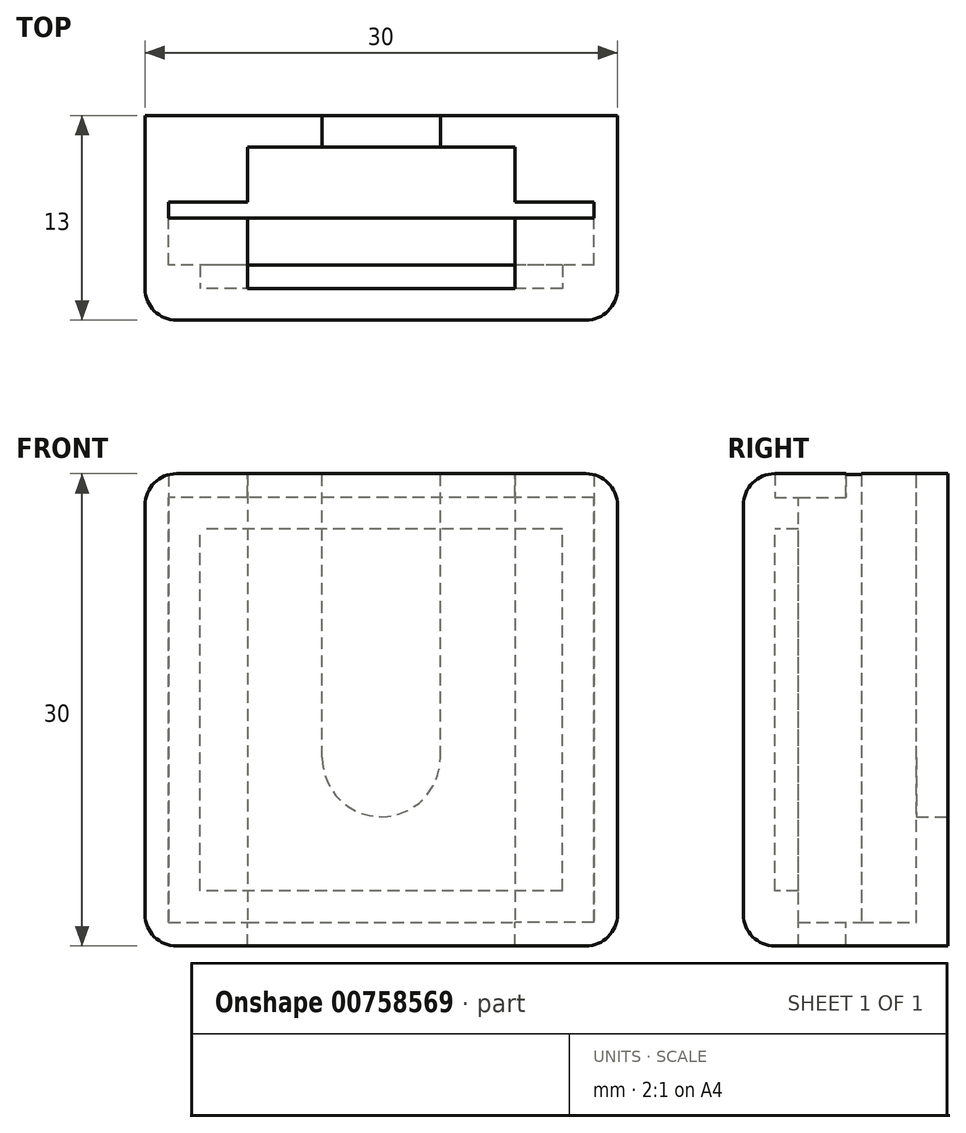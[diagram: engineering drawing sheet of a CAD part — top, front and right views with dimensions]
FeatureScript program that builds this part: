
annotation { "Feature Type Name" : "Feature", "Feature Type Description" : "" }
export const myFeature = defineFeature(function(context is Context, id is Id, definition is map)
    precondition{}
    {
        {
            var Q0;
            Q0=qCreatedBy(makeId("Front.planeOp"),FACE);
            var sketch = newSketch(context, id + "F0", { "sketchPlane" : qUnion([Q0])});
            skLineSegment(sketch, "E0.bottom", {"start": v(13.5, -13.5) * mm, "end": v(-13.5, -13.5) * mm});
            skLineSegment(sketch, "E0.top", {"start": v(13.5, 13.5) * mm, "end": v(-13.5, 13.5) * mm});
            skLineSegment(sketch, "E0.left", {"start": v(13.5, -13.5) * mm, "end": v(13.5, 13.5) * mm});
            skLineSegment(sketch, "E0.right", {"start": v(-13.5, -13.5) * mm, "end": v(-13.5, 13.5) * mm});
            skPoint(sketch, "E0.middle", {"position": v(0, 0) * mm});
            skLineSegment(sketch, "E1.0", {"start": v(15, 15) * mm, "end": v(-15, 15) * mm});
            skLineSegment(sketch, "E1.1", {"start": v(15, -15) * mm, "end": v(15, 15) * mm});
            skLineSegment(sketch, "E1.2", {"start": v(15, -15) * mm, "end": v(-15, -15) * mm});
            skLineSegment(sketch, "E1.3", {"start": v(-15, -15) * mm, "end": v(-15, 15) * mm});
            skCircle(sketch, "E2", {"center": v(0, -3.04) * mm, "radius": 3.75 * mm});
            skLineSegment(sketch, "E3", {"start": v(0, -3.04) * mm, "end": v(-3.75, -3.04) * mm, "construction": true});
            skLineSegment(sketch, "E4", {"start": v(0, -3.04) * mm, "end": v(3.75, -3.04) * mm, "construction": true});
            skLineSegment(sketch, "E5", {"start": v(3.75, -3.04) * mm, "end": v(3.75, 15) * mm});
            skLineSegment(sketch, "E6", {"start": v(-3.75, -3.04) * mm, "end": v(-3.75, 15) * mm});
            skLineSegment(sketch, "E7", {"start": v(-8.5, 15) * mm, "end": v(-8.5, -13.5) * mm});
            skLineSegment(sketch, "E8", {"start": v(8.5, 15) * mm, "end": v(8.5, -13.5) * mm});
            skSolve(sketch);
        }
        {
            var Q0;
            Q0=makeQuery(id+"F0.imprint","IMPRINT",FACE,{"disambiguationData":[TD([[makeQuery(id+"F0.imprint","IMPRINT",EDGE,{"derivedFrom":sQuery(id+"F0.wireOp",EDGE,"E0.bottom")}),-1.0]])]});
            var Q1;
            Q1=makeQuery(id+"F0.imprint","IMPRINT",FACE,{"disambiguationData":[TD([[makeQuery(id+"F0.imprint","IMPRINT",EDGE,{"derivedFrom":sQuery(id+"F0.wireOp",EDGE,"E0.bottom")}),1.0]])]});
            var Q2;
            {var subQ5=sQuery(id+"F0.wireOp",EDGE,"E7");Q2=makeQuery(id+"F0.imprint","IMPRINT",FACE,{"disambiguationData":[TD([[makeQuery(id+"F0.imprint","IMPRINT",EDGE,{"derivedFrom":subQ5}),1.0]])]});}
            var Q3;
            {var subQ0=sQuery(id+"F0.wireOp",EDGE,"E8");var subQ1=sQuery(id+"F0.wireOp",EDGE,"E0.top");var subQ2=makeQuery(id+"F0.imprint","INTERSECT",VERTEX,{"derivedFrom":[subQ1,subQ0]});Q3=makeQuery(id+"F0.imprint","IMPRINT",FACE,{"disambiguationData":[TD([[makeQuery(id+"F0.imprint","IMPRINT",EDGE,{"disambiguationData":[TD([[subQ2,-1.0]])],"derivedFrom":subQ1}),-1.0]])]});}
            var Q4;
            {var subQ10=sQuery(id+"F0.wireOp",EDGE,"E7");var subQ12=sQuery(id+"F0.wireOp",EDGE,"E0.bottom");var subQ13=makeQuery(id+"F0.imprint","INTERSECT",VERTEX,{"derivedFrom":[subQ12,subQ10]});Q4=makeQuery(id+"F0.imprint","IMPRINT",FACE,{"disambiguationData":[TD([[makeQuery(id+"F0.imprint","IMPRINT",EDGE,{"disambiguationData":[TD([[subQ13,1.0]])],"derivedFrom":subQ12}),-1.0]])]});}
            extrude(context, id + "F1", {"entities" : qUnion([Q0, Q1, Q2, Q3, Q4]), "depth" : 2 * mm, "offsetDistance" : 25 * mm});
        }
        {
            var Q0;
            {var subQ0=sQuery(id+"F0.wireOp",EDGE,"E0.right");Q0=makeQuery(id+"F0.imprint","IMPRINT",FACE,{"disambiguationData":[TD([[makeQuery(id+"F0.imprint","IMPRINT",EDGE,{"derivedFrom":subQ0}),-1.0]])]});}
            var Q1;
            {var subQ0=sQuery(id+"F0.wireOp",EDGE,"E0.left");Q1=makeQuery(id+"F0.imprint","IMPRINT",FACE,{"disambiguationData":[TD([[makeQuery(id+"F0.imprint","IMPRINT",EDGE,{"derivedFrom":subQ0}),1.0]])]});}
            var Q2;
            {var subQ5=sQuery(id+"F0.wireOp",EDGE,"E0.left");Q2=makeQuery(id+"F0.imprint","IMPRINT",FACE,{"disambiguationData":[TD([[makeQuery(id+"F0.imprint","IMPRINT",EDGE,{"derivedFrom":subQ5}),-1.0]])]});}
            extrude(context, id + "F2", {"entities" : qUnion([Q0, Q1, Q2]), "operationType" : NewBodyOperationType.ADD, "depth" : 5.5 * mm, "offsetDistance" : 25 * mm});
        }
        {
            var Q0;
            {var subQ5=sQuery(id+"F0.wireOp",EDGE,"E0.left");Q0=makeQuery(id+"F0.imprint","IMPRINT",FACE,{"disambiguationData":[TD([[makeQuery(id+"F0.imprint","IMPRINT",EDGE,{"derivedFrom":subQ5}),-1.0]])]});}
            extrude(context, id + "F3", {"entities" : qUnion([Q0]), "operationType" : NewBodyOperationType.ADD, "depth" : 11 * mm, "offsetDistance" : 25 * mm});
        }
        {
            var Q0;
            {var subQ0=sQuery(id+"F0.wireOp",EDGE,"E0.bottom");Q0=makeQuery(id+"F3.boolean.opBoolean","MERGE",FACE,{"derivedFrom":[makeQuery(id+"F2.boolean.opBoolean","MERGE",FACE,{"derivedFrom":[makeQuery(id+"F1.opExtrude","SWEPT_FACE",FACE,{"disambiguationData":[OSD([subQ0])]}),makeQuery(id+"F2.opExtrude","SWEPT_FACE",FACE,{"disambiguationData":[OSD([subQ0])]})]}),makeQuery(id+"F3.opExtrude","SWEPT_FACE",FACE,{"disambiguationData":[OSD([subQ0])]})]});}
            var sketch = newSketch(context, id + "F4", { "sketchPlane" : qUnion([Q0])});
            skLineSegment(sketch, "E9", {"start": v(-13.5, -6.5) * mm, "end": v(13.5, -6.5) * mm});
            skLineSegment(sketch, "E10", {"start": v(-8.5, -5.5) * mm, "end": v(8.5, -5.5) * mm});
            skLineSegment(sketch, "E11", {"start": v(0, -6.5) * mm, "end": v(0, -11) * mm, "construction": true});
            skLineSegment(sketch, "E12.bottom", {"start": v(8.5, -9.5) * mm, "end": v(-8.5, -9.5) * mm});
            skLineSegment(sketch, "E12.top", {"start": v(8.5, -6.5) * mm, "end": v(-8.5, -6.5) * mm});
            skLineSegment(sketch, "E12.left", {"start": v(8.5, -9.5) * mm, "end": v(8.5, -6.5) * mm});
            skLineSegment(sketch, "E12.right", {"start": v(-8.5, -9.5) * mm, "end": v(-8.5, -6.5) * mm});
            skPoint(sketch, "E12.middle", {"position": v(0, -8) * mm});
            skSolve(sketch);
        }
        {
            var Q0;
            Q0=makeQuery(id+"F4.imprint","IMPRINT",FACE,{"disambiguationData":[TD([[makeQuery(id+"F4.imprint","IMPRINT",EDGE,{"derivedFrom":sQuery(id+"F4.wireOp",EDGE,"E10")}),-1.0]])]});
            var Q1;
            {var subQ0=sQuery(id+"F0.wireOp",EDGE,"E1.0");var subQ2=makeQuery(id+"F0.imprint","IMPRINT",EDGE,{"disambiguationData":[TD([[makeQuery(id+"F0.imprint","INTERSECT",VERTEX,{"derivedFrom":[subQ0,sQuery(id+"F0.wireOp",EDGE,"E1.3")]}),1.0]])],"derivedFrom":subQ0});Q1=makeQuery(id+"F3.boolean.opBoolean","MERGE",FACE,{"derivedFrom":[makeQuery(id+"F2.boolean.opBoolean","MERGE",FACE,{"derivedFrom":[makeQuery(id+"F1.opExtrude","SWEPT_FACE",FACE,{"disambiguationData":[OSD([subQ0]),TDD([makeQuery(id+"F0.imprint","IMPRINT",EDGE,{"disambiguationData":[TD([[makeQuery(id+"F0.imprint","INTERSECT",VERTEX,{"derivedFrom":[subQ0,sQuery(id+"F0.wireOp",EDGE,"E6")]}),-1.0]])],"derivedFrom":subQ0}),subQ2])]}),makeQuery(id+"F2.opExtrude","SWEPT_FACE",FACE,{"disambiguationData":[OSD([subQ0]),TDD([subQ2])]})]}),makeQuery(id+"F3.opExtrude","SWEPT_FACE",FACE,{"disambiguationData":[OSD([subQ0]),TDD([subQ2])]})]});}
            extrude(context, id + "F5", {"entities" : qUnion([Q0]), "operationType" : NewBodyOperationType.REMOVE, "endBound" : BoundingType.UP_TO_SURFACE, "depth" : 25 * mm, "endBoundEntityFace" : qUnion([Q1]), "offsetDistance" : 25 * mm});
        }
        {
            var Q0;
            Q0=makeQuery(id+"F4.imprint","IMPRINT",FACE,{"disambiguationData":[TD([[makeQuery(id+"F4.imprint","IMPRINT",EDGE,{"derivedFrom":sQuery(id+"F4.wireOp",EDGE,"E12.bottom")}),-1.0]])]});
            var Q1;
            {var subQ0=sQuery(id+"F0.wireOp",EDGE,"E1.2");Q1=makeQuery(id+"F3.boolean.opBoolean","MERGE",FACE,{"derivedFrom":[makeQuery(id+"F2.boolean.opBoolean","MERGE",FACE,{"derivedFrom":[makeQuery(id+"F1.opExtrude","SWEPT_FACE",FACE,{"disambiguationData":[OSD([subQ0])]}),makeQuery(id+"F2.opExtrude","SWEPT_FACE",FACE,{"disambiguationData":[OSD([subQ0])]})]}),makeQuery(id+"F3.opExtrude","SWEPT_FACE",FACE,{"disambiguationData":[OSD([subQ0])]})]});}
            extrude(context, id + "F6", {"entities" : qUnion([Q0]), "operationType" : NewBodyOperationType.REMOVE, "endBound" : BoundingType.UP_TO_SURFACE, "oppositeDirection" : true, "depth" : 25 * mm, "endBoundEntityFace" : qUnion([Q1]), "offsetDistance" : 25 * mm});
        }
        {
            var Q0;
            Q0=makeQuery(id+"F3.opExtrude","CAP_FACE",FACE,{"disambiguationData":[OSD([sQuery(id+"F0.wireOp",EDGE,"E0.bottom"),sQuery(id+"F0.wireOp",EDGE,"E0.top"),sQuery(id+"F0.wireOp",EDGE,"E0.left"),sQuery(id+"F0.wireOp",EDGE,"E0.right"),sQuery(id+"F0.wireOp",EDGE,"E1.0"),sQuery(id+"F0.wireOp",EDGE,"E1.1"),sQuery(id+"F0.wireOp",EDGE,"E1.2"),sQuery(id+"F0.wireOp",EDGE,"E1.3"),sQuery(id+"F0.wireOp",EDGE,"E7"),sQuery(id+"F0.wireOp",EDGE,"E8")])],"isStart":false});
            var sketch = newSketch(context, id + "F7", { "sketchPlane" : qUnion([Q0])});
            skLineSegment(sketch, "E13.bottom", {"start": v(15, -15) * mm, "end": v(-15, -15) * mm});
            skLineSegment(sketch, "E13.top", {"start": v(15, 15) * mm, "end": v(-15, 15) * mm});
            skLineSegment(sketch, "E13.left", {"start": v(15, -15) * mm, "end": v(15, 15) * mm});
            skLineSegment(sketch, "E13.right", {"start": v(-15, -15) * mm, "end": v(-15, 15) * mm});
            skPoint(sketch, "E13.middle", {"position": v(0, 0) * mm});
            skLineSegment(sketch, "E14.bottom", {"start": v(13.5, -13.5) * mm, "end": v(-13.5, -13.5) * mm});
            skLineSegment(sketch, "E14.top", {"start": v(13.5, 13.5) * mm, "end": v(-13.5, 13.5) * mm});
            skLineSegment(sketch, "E14.left", {"start": v(13.5, -13.5) * mm, "end": v(13.5, 13.5) * mm});
            skLineSegment(sketch, "E14.right", {"start": v(-13.5, -13.5) * mm, "end": v(-13.5, 13.5) * mm});
            skLineSegment(sketch, "E15.0", {"start": v(-11.5, -11.5) * mm, "end": v(-11.5, 11.5) * mm});
            skLineSegment(sketch, "E15.1", {"start": v(11.5, -11.5) * mm, "end": v(-11.5, -11.5) * mm});
            skLineSegment(sketch, "E15.2", {"start": v(11.5, -11.5) * mm, "end": v(11.5, 11.5) * mm});
            skLineSegment(sketch, "E15.3", {"start": v(11.5, 11.5) * mm, "end": v(-11.5, 11.5) * mm});
            skSolve(sketch);
        }
        {
            var Q0;
            Q0 = qSketchRegion(id + "F7", true);
            var Q1;
            Q1=makeQuery(id+"F7.imprint","IMPRINT",FACE,{"disambiguationData":[TD([[makeQuery(id+"F7.imprint","IMPRINT",EDGE,{"derivedFrom":sQuery(id+"F7.wireOp",EDGE,"E14.bottom")}),-1.0]])]});
            var Q2;
            Q2=makeQuery(id+"F7.imprint","IMPRINT",FACE,{"disambiguationData":[TD([[makeQuery(id+"F7.imprint","IMPRINT",EDGE,{"derivedFrom":sQuery(id+"F7.wireOp",EDGE,"E15.0")}),-1.0]])]});
            extrude(context, id + "F8", {"entities" : qUnion([Q0, Q1, Q2]), "depth" : 2 * mm, "offsetDistance" : 25 * mm});
        }
        {
            var Q0;
            Q0=makeQuery(id+"F7.imprint","IMPRINT",FACE,{"disambiguationData":[TD([[makeQuery(id+"F7.imprint","IMPRINT",EDGE,{"derivedFrom":sQuery(id+"F7.wireOp",EDGE,"E14.bottom")}),-1.0]])]});
            extrude(context, id + "F9", {"entities" : qUnion([Q0]), "operationType" : NewBodyOperationType.ADD, "depth" : -1.5 * mm, "offsetDistance" : 25 * mm});
        }
        {
            var Q0;
            Q0=makeQuery(id+"F8.opExtrude","CAP_EDGE",EDGE,{"disambiguationData":[OSD([sQuery(id+"F7.wireOp",EDGE,"E13.top")])],"isStart":false});
            var Q1;
            Q1=makeQuery(id+"F8.opExtrude","CAP_EDGE",EDGE,{"disambiguationData":[OSD([sQuery(id+"F7.wireOp",EDGE,"E13.left")])],"isStart":false});
            var Q2;
            Q2=makeQuery(id+"F8.opExtrude","CAP_EDGE",EDGE,{"disambiguationData":[OSD([sQuery(id+"F7.wireOp",EDGE,"E13.bottom")])],"isStart":false});
            var Q3;
            Q3=makeQuery(id+"F8.opExtrude","CAP_EDGE",EDGE,{"disambiguationData":[OSD([sQuery(id+"F7.wireOp",EDGE,"E13.right")])],"isStart":false});
            var Q4;
            Q4=makeQuery(id+"F8.opExtrude","SWEPT_EDGE",EDGE,{"disambiguationData":[OSD([sQuery(id+"F7.wireOp",EDGE,"E13.top"),sQuery(id+"F7.wireOp",EDGE,"E13.left")])]});
            var Q5;
            Q5=makeQuery(id+"F8.opExtrude","SWEPT_EDGE",EDGE,{"disambiguationData":[OSD([sQuery(id+"F7.wireOp",EDGE,"E13.top"),sQuery(id+"F7.wireOp",EDGE,"E13.right")])]});
            var Q6;
            Q6=makeQuery(id+"F8.opExtrude","SWEPT_EDGE",EDGE,{"disambiguationData":[OSD([sQuery(id+"F7.wireOp",EDGE,"E13.bottom"),sQuery(id+"F7.wireOp",EDGE,"E13.left")])]});
            var Q7;
            Q7=makeQuery(id+"F8.opExtrude","SWEPT_EDGE",EDGE,{"disambiguationData":[OSD([sQuery(id+"F7.wireOp",EDGE,"E13.bottom"),sQuery(id+"F7.wireOp",EDGE,"E13.right")])]});
            var Q8;
            {var subQ0=sQuery(id+"F0.wireOp",EDGE,"E1.2");var subQ1=sQuery(id+"F0.wireOp",EDGE,"E1.1");Q8=makeQuery(id+"F3.boolean.opBoolean","MERGE",EDGE,{"derivedFrom":[makeQuery(id+"F2.boolean.opBoolean","MERGE",EDGE,{"derivedFrom":[makeQuery(id+"F1.opExtrude","SWEPT_EDGE",EDGE,{"disambiguationData":[OSD([subQ1,subQ0])]}),makeQuery(id+"F2.opExtrude","SWEPT_EDGE",EDGE,{"disambiguationData":[OSD([subQ1,subQ0])]})]}),makeQuery(id+"F3.opExtrude","SWEPT_EDGE",EDGE,{"disambiguationData":[OSD([subQ1,subQ0])]})]});}
            var Q9;
            {var subQ0=sQuery(id+"F0.wireOp",EDGE,"E1.1");var subQ1=sQuery(id+"F0.wireOp",EDGE,"E1.0");Q9=makeQuery(id+"F3.boolean.opBoolean","MERGE",EDGE,{"derivedFrom":[makeQuery(id+"F2.boolean.opBoolean","MERGE",EDGE,{"derivedFrom":[makeQuery(id+"F1.opExtrude","SWEPT_EDGE",EDGE,{"disambiguationData":[OSD([subQ1,subQ0])]}),makeQuery(id+"F2.opExtrude","SWEPT_EDGE",EDGE,{"disambiguationData":[OSD([subQ1,subQ0])]})]}),makeQuery(id+"F3.opExtrude","SWEPT_EDGE",EDGE,{"disambiguationData":[OSD([subQ1,subQ0])]})]});}
            var Q10;
            {var subQ0=sQuery(id+"F0.wireOp",EDGE,"E1.3");var subQ1=sQuery(id+"F0.wireOp",EDGE,"E1.0");Q10=makeQuery(id+"F3.boolean.opBoolean","MERGE",EDGE,{"derivedFrom":[makeQuery(id+"F2.boolean.opBoolean","MERGE",EDGE,{"derivedFrom":[makeQuery(id+"F1.opExtrude","SWEPT_EDGE",EDGE,{"disambiguationData":[OSD([subQ1,subQ0])]}),makeQuery(id+"F2.opExtrude","SWEPT_EDGE",EDGE,{"disambiguationData":[OSD([subQ1,subQ0])]})]}),makeQuery(id+"F3.opExtrude","SWEPT_EDGE",EDGE,{"disambiguationData":[OSD([subQ1,subQ0])]})]});}
            var Q11;
            {var subQ0=sQuery(id+"F0.wireOp",EDGE,"E1.3");var subQ1=sQuery(id+"F0.wireOp",EDGE,"E1.2");Q11=makeQuery(id+"F3.boolean.opBoolean","MERGE",EDGE,{"derivedFrom":[makeQuery(id+"F2.boolean.opBoolean","MERGE",EDGE,{"derivedFrom":[makeQuery(id+"F1.opExtrude","SWEPT_EDGE",EDGE,{"disambiguationData":[OSD([subQ1,subQ0])]}),makeQuery(id+"F2.opExtrude","SWEPT_EDGE",EDGE,{"disambiguationData":[OSD([subQ1,subQ0])]})]}),makeQuery(id+"F3.opExtrude","SWEPT_EDGE",EDGE,{"disambiguationData":[OSD([subQ1,subQ0])]})]});}
            fillet(context, id + "F10", {"entities" : qUnion([Q0, Q1, Q2, Q3, Q4, Q5, Q6, Q7, Q8, Q9, Q10, Q11]), "radius" : 2 * mm, "tangentPropagation" : true, "allowEdgeOverflow" : false});
        }
    });
